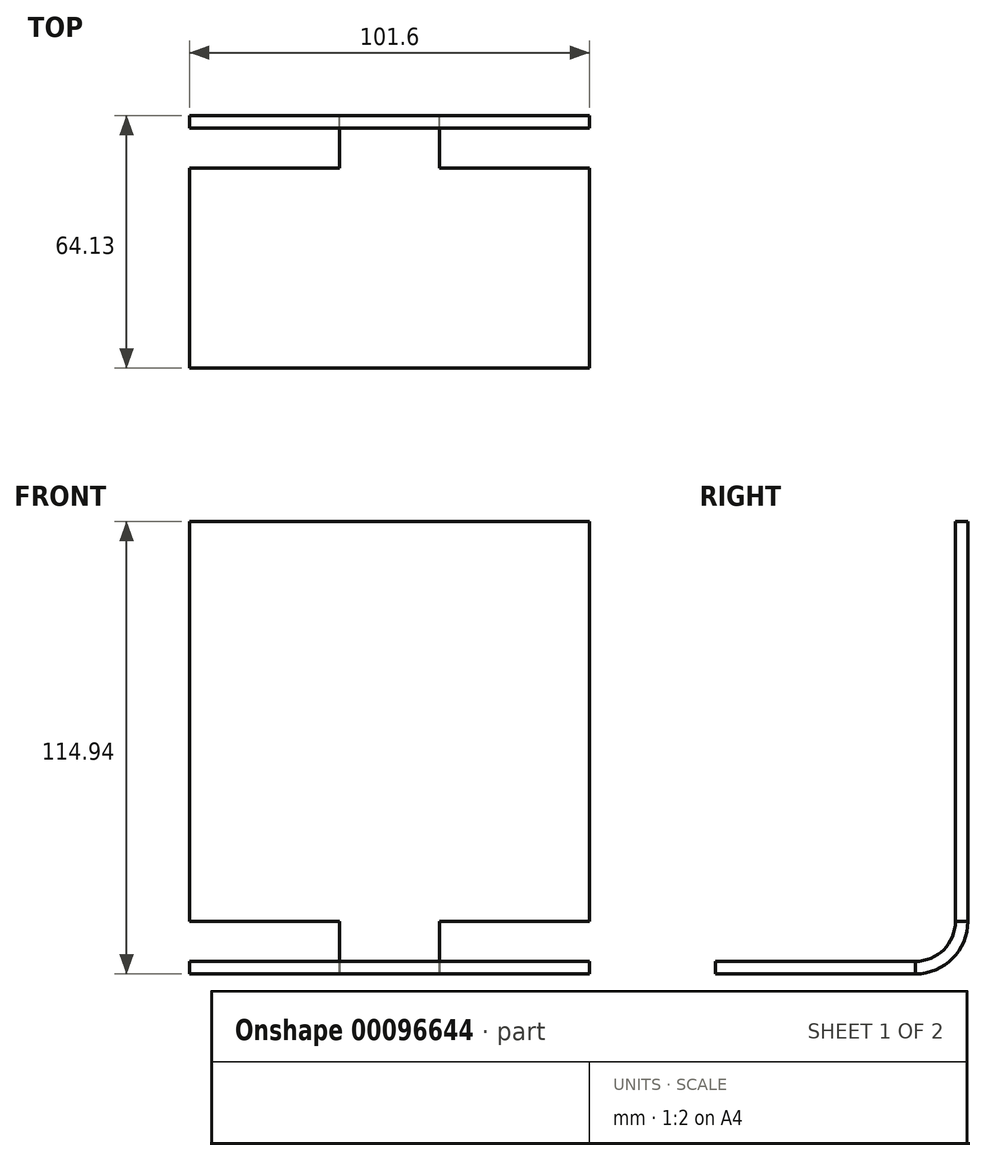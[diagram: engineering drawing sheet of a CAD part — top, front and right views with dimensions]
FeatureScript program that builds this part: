
annotation { "Feature Type Name" : "Feature", "Feature Type Description" : "" }
export const myFeature = defineFeature(function(context is Context, id is Id, definition is map)
    precondition{}
    {
        {
            var Q0;
            Q0=qCreatedBy(makeId("Top.planeOp"),FACE);
            var sketch = newSketch(context, id + "F0", { "sketchPlane" : qUnion([Q0])});
            skLineSegment(sketch, "E0.bottom", {"start": v(0, 0) * mm, "end": v(101.6, 0) * mm});
            skLineSegment(sketch, "E0.top", {"start": v(0, 50.8) * mm, "end": v(101.6, 50.8) * mm});
            skLineSegment(sketch, "E0.left", {"start": v(0, 0) * mm, "end": v(0, 50.8) * mm});
            skLineSegment(sketch, "E0.right", {"start": v(101.6, 0) * mm, "end": v(101.6, 50.8) * mm});
            skSolve(sketch);
        }
        {
            var Q0;
            Q0 = qSketchRegion(id + "F0", true);
            extrude(context, id + "F1", {"entities" : qUnion([Q0]), "depth" : 3.17 * mm});
        }
        {
            var Q0;
            Q0=qCreatedBy(makeId("Top.planeOp"),FACE);
            var sketch = newSketch(context, id + "F2", { "sketchPlane" : qUnion([Q0])});
            skPoint(sketch, "E1", {"position": v(50.8, 50.8) * mm});
            skSolve(sketch);
        }
        {
            var Q0;
            Q0=qCreatedBy(makeId("Right.planeOp"),FACE);
            var Q1;
            Q1=sQuery(id+"F2.wireOp",VERTEX,"E1");
            cPlane(context, id + "F3", {"entities" : qUnion([Q0, Q1]), "cplaneType" : CPlaneType.PLANE_POINT, "offset" : 152.4 * mm, "width" : 152.4 * mm, "height" : 152.4 * mm});
        }
        {
            var Q0;
            Q0=qCreatedBy(id+"F3.planeOp",FACE);
            var sketch = newSketch(context, id + "F4", { "sketchPlane" : qUnion([Q0])});
            skArc(sketch, "E2", {"start": v(50.8, 3.18) * mm, "mid": v(57.98, 6.15) * mm, "end": v(60.96, 13.34) * mm});
            skArc(sketch, "E3", {"start": v(50.8, 0) * mm, "mid": v(60.23, 3.9) * mm, "end": v(64.13, 13.34) * mm});
            skLineSegment(sketch, "E4", {"start": v(50.8, 3.17) * mm, "end": v(50.8, 0) * mm});
            skLineSegment(sketch, "E5", {"start": v(60.96, 13.34) * mm, "end": v(64.13, 13.34) * mm});
            skSolve(sketch);
        }
        {
            var Q0;
            Q0 = qSketchRegion(id + "F4", true);
            extrude(context, id + "F5", {"entities" : qUnion([Q0]), "operationType" : NewBodyOperationType.ADD, "depth" : 12.7 * mm, "hasSecondDirection" : true, "secondDirectionOppositeDirection" : true, "secondDirectionDepth" : 12.7 * mm});
        }
        {
            var Q0;
            Q0=qCreatedBy(id+"F3.planeOp",FACE);
            var sketch = newSketch(context, id + "F6", { "sketchPlane" : qUnion([Q0])});
            skPoint(sketch, "E6", {"position": v(60.96, 13.34) * mm});
            skSolve(sketch);
        }
        {
            var Q0;
            Q0=qCreatedBy(makeId("Front.planeOp"),FACE);
            var Q1;
            Q1=sQuery(id+"F6.wireOp",VERTEX,"E6");
            cPlane(context, id + "F7", {"entities" : qUnion([Q0, Q1]), "cplaneType" : CPlaneType.PLANE_POINT, "offset" : 152.4 * mm, "width" : 152.4 * mm, "height" : 152.4 * mm});
        }
        {
            var Q0;
            Q0=qCreatedBy(id+"F7.planeOp",FACE);
            var sketch = newSketch(context, id + "F8", { "sketchPlane" : qUnion([Q0])});
            skLineSegment(sketch, "E7.bottom", {"start": v(0, 13.34) * mm, "end": v(101.6, 13.34) * mm});
            skLineSegment(sketch, "E7.top", {"start": v(0, 114.94) * mm, "end": v(101.6, 114.94) * mm});
            skLineSegment(sketch, "E7.left", {"start": v(0, 13.34) * mm, "end": v(0, 114.94) * mm});
            skLineSegment(sketch, "E7.right", {"start": v(101.6, 13.33) * mm, "end": v(101.6, 114.94) * mm});
            skSolve(sketch);
        }
        {
            var Q0;
            Q0 = qSketchRegion(id + "F8", true);
            extrude(context, id + "F9", {"entities" : qUnion([Q0]), "operationType" : NewBodyOperationType.ADD, "oppositeDirection" : true, "depth" : 3.17 * mm});
        }
    });
